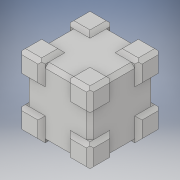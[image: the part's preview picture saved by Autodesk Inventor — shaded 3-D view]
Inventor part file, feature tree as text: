
AUTODESK INVENTOR PART (.ipt)
format: ipt  version: 2018 (Build 220112000, 112)  size: 468,480 bytes
history: native  units: in
note: dims shown in document units (in); Inventor stores cm internally (conversion verified against a paired STEP export)
features: chamfer x76, extrude x6, sketch x6
ambient origin geometry x8: Origin, YZ Plane, XZ Plane, XY Plane, X Axis, Y Axis, Z Axis, Center Point
bodies: Solid1 (feature_tree)
feature tree (88):
  extrude  "Extrusion1"  Depth=4.0in
  extrude  "Extrusion2"  Depth=1.3in
  extrude  "Extrusion3"  Depth=1.3in
  extrude  "Extrusion4"  Depth=1.3in
  extrude  "Extrusion5"  Depth=1.3in
  extrude  "Extrusion6"  Depth=1.3in
  chamfer  "Chamfer42"  Distance=1.3in
  chamfer  "Chamfer43"  Distance=1.3in
  chamfer  "Chamfer44"  Distance=1.3in
  chamfer  "Chamfer45"  Distance=0.2in
  chamfer  "Chamfer46"  Distance=0.2in
  chamfer  "Chamfer47"  Distance=0.2in
  chamfer  "Chamfer48"  Distance=0.2in
  chamfer  "Chamfer49"  Distance=0.2in Angle=45.0deg
  chamfer  "Chamfer50"  Distance=0.2in Angle=45.0deg
  chamfer  "Chamfer51"  Distance=0.2in Angle=45.0deg
  chamfer  "Chamfer52"  Distance=0.2in Angle=45.0deg
  chamfer  "Chamfer53"  Distance=0.2in Angle=45.0deg
  chamfer  "Chamfer54"  Distance=0.2in Angle=45.0deg
  chamfer  "Chamfer55"  Distance=0.2in Angle=45.0deg
  chamfer  "Chamfer56"  Distance=0.2in Angle=45.0deg
  chamfer  "Chamfer57"  Distance=0.2in Angle=45.0deg
  chamfer  "Chamfer58"  Distance=0.2in Angle=45.0deg
  chamfer  "Chamfer59"  Distance=0.2in Angle=45.0deg
  chamfer  "Chamfer60"  Distance=0.2in Angle=45.0deg
  chamfer  "Chamfer61"  Distance=0.2in Angle=45.0deg
  chamfer  "Chamfer62"  Distance=0.2in Angle=45.0deg
  chamfer  "Chamfer63"  Distance=0.2in Angle=45.0deg
  chamfer  "Chamfer64"  Distance=0.2in Angle=45.0deg
  chamfer  "Chamfer65"  Distance=0.2in Angle=45.0deg
  chamfer  "Chamfer66"  Distance=0.2in Angle=45.0deg
  chamfer  "Chamfer67"  Distance=0.2in Angle=45.0deg
  chamfer  "Chamfer68"  Distance=0.2in Angle=45.0deg
  chamfer  "Chamfer69"  Distance=0.2in Angle=45.0deg
  chamfer  "Chamfer70"  Distance=0.2in Angle=45.0deg
  chamfer  "Chamfer71"  Distance=0.2in Angle=45.0deg
  chamfer  "Chamfer72"  Distance=0.2in Angle=45.0deg
  chamfer  "Chamfer73"  Distance=0.2in Angle=45.0deg
  chamfer  "Chamfer74"  Distance=0.2in Angle=45.0deg
  chamfer  "Chamfer75"  Distance=0.2in Angle=45.0deg
  chamfer  "Chamfer76"  Distance=0.2in Angle=45.0deg
  chamfer  "Chamfer77"  Distance=0.2in Angle=45.0deg
  chamfer  "Chamfer78"  Distance=0.2in Angle=45.0deg
  chamfer  "Chamfer79"  Distance=0.2in Angle=45.0deg
  chamfer  "Chamfer80"  Distance=0.2in Angle=45.0deg
  chamfer  "Chamfer81"  Distance=0.2in Angle=45.0deg
  chamfer  "Chamfer82"  Distance=0.2in Angle=45.0deg
  chamfer  "Chamfer83"  Distance=0.2in Angle=45.0deg
  chamfer  "Chamfer84"  Distance=0.2in Angle=45.0deg
  chamfer  "Chamfer85"  Distance=0.2in Angle=45.0deg
  chamfer  "Chamfer86"  Distance=0.2in Angle=45.0deg
  chamfer  "Chamfer87"  Distance=0.2in Angle=45.0deg
  chamfer  "Chamfer88"  Distance=0.2in Angle=45.0deg
  chamfer  "Chamfer89"  Distance=0.2in Angle=45.0deg
  chamfer  "Chamfer90"  Distance=0.2in Angle=45.0deg
  chamfer  "Chamfer91"  Distance=0.2in Angle=45.0deg
  chamfer  "Chamfer92"  Distance=0.2in Angle=45.0deg
  chamfer  "Chamfer93"  Distance=0.2in Angle=45.0deg
  chamfer  "Chamfer94"  Distance=0.2in Angle=45.0deg
  chamfer  "Chamfer95"  Distance=0.2in Angle=45.0deg
  chamfer  "Chamfer96"  Distance=0.2in Angle=45.0deg
  chamfer  "Chamfer97"  Distance=0.2in Angle=45.0deg
  chamfer  "Chamfer98"  Distance=0.2in Angle=45.0deg
  chamfer  "Chamfer99"  Distance=0.2in Angle=45.0deg
  chamfer  "Chamfer100"  Distance=0.2in Angle=45.0deg
  chamfer  "Chamfer101"  Distance=0.2in Angle=45.0deg
  chamfer  "Chamfer102"  Distance=0.2in Angle=45.0deg
  chamfer  "Chamfer103"  Distance=0.2in Angle=45.0deg
  chamfer  "Chamfer104"  Distance=0.2in Angle=45.0deg
  chamfer  "Chamfer105"  Distance=0.2in Angle=45.0deg
  chamfer  "Chamfer106"  Distance=0.2in Angle=45.0deg
  chamfer  "Chamfer107"  Distance=0.2in Angle=45.0deg
  chamfer  "Chamfer108"  Distance=0.2in Angle=45.0deg
  chamfer  "Chamfer109"  Distance=0.2in Angle=45.0deg
  chamfer  "Chamfer110"  Distance=0.2in Angle=45.0deg
  chamfer  "Chamfer111"  Distance=0.2in Angle=45.0deg
  chamfer  "Chamfer112"  Distance=0.2in Angle=45.0deg
  chamfer  "Chamfer113"  Distance=0.2in Angle=45.0deg
  chamfer  "Chamfer114"  Distance=0.2in Angle=45.0deg
  chamfer  "Chamfer115"  Distance=0.2in Angle=45.0deg
  chamfer  "Chamfer116"  Distance=0.2in Angle=45.0deg
  chamfer  "Chamfer117"  Distance=0.2in Angle=45.0deg
  sketch  "Sketch1"  dims[d0=4.0in d1=4.0in]
  sketch  "Sketch2"  dims[d2=4.0in d3=0.0in d4=1.3in]
  sketch  "Sketch3"  dims[d5=1.3in d6=1.3in]
  sketch  "Sketch4"  dims[d7=1.3in d8=1.3in]
  sketch  "Sketch5"  dims[d9=1.3in d10=1.3in]
  sketch  "Sketch6"  dims[d11=0.2in d12=0.0in d13=1.3in d14=1.3in d15=1.3in d16=1.3in d17=0.2in d18=0.0in d19=0.2in d20=0.0in d21=0.2in d22=0.0in d23=0.2in d24=0.0in d148=0.2in d149=0.2in d150=45.0deg d151=0.2in d152=0.2in d153=45.0deg d154=0.2in d155=0.2in d156=45.0deg d157=0.2in d158=0.2in d159=45.0deg d160=0.2in d161=0.2in d162=45.0deg d163=0.2in d164=0.2in d165=45.0deg d166=0.2in d167=0.2in d168=45.0deg d169=0.2in d170=0.2in d171=45.0deg d172=0.2in d173=0.2in d174=45.0deg d175=0.2in d176=0.2in d177=45.0deg d178=0.2in d179=0.2in d180=45.0deg d181=0.2in d182=0.2in d183=45.0deg d184=0.2in d185=0.2in d186=45.0deg d187=0.2in d188=0.2in d189=45.0deg d190=0.2in d191=0.2in d192=45.0deg d193=0.2in d194=0.2in d195=45.0deg d196=0.2in d197=0.2in d198=45.0deg d199=0.2in d200=0.2in d201=45.0deg d202=0.2in d203=0.2in d204=45.0deg d205=0.2in d206=0.2in d207=45.0deg d208=0.2in d209=0.2in d210=45.0deg d211=0.2in d212=0.2in d213=45.0deg d214=0.2in d215=0.2in d216=45.0deg d217=0.2in d218=0.2in d219=45.0deg d220=0.2in d221=0.2in d222=45.0deg d223=0.2in d224=0.2in d225=45.0deg d226=0.2in d227=0.2in d228=45.0deg d229=0.2in d230=0.2in d231=45.0deg d232=0.2in d233=0.2in d234=45.0deg d235=0.2in d236=0.2in d237=45.0deg d238=0.2in d239=0.2in d240=45.0deg d241=0.2in d242=0.2in d243=45.0deg d244=0.2in d245=0.2in d246=45.0deg d247=0.2in d248=0.2in d249=45.0deg d250=0.2in d251=0.2in d252=45.0deg d253=0.2in d254=0.2in d255=45.0deg d256=0.2in d257=0.2in d258=45.0deg d259=0.2in d260=0.2in d261=45.0deg d262=0.2in d263=0.2in d264=45.0deg d265=0.2in d266=0.2in d267=45.0deg d268=0.2in d269=0.2in d270=45.0deg d271=0.2in d272=0.2in d273=45.0deg d274=0.2in d275=0.2in d276=45.0deg d277=0.2in d278=0.2in d279=45.0deg d280=0.2in d281=0.2in d282=45.0deg d283=0.2in d284=0.2in d285=45.0deg d286=0.2in d287=0.2in d288=45.0deg d289=0.2in d290=0.2in d291=45.0deg d292=0.2in d293=0.2in d294=45.0deg d295=0.2in d296=0.2in d297=45.0deg d298=0.2in d299=0.2in d300=45.0deg d301=0.2in d302=0.2in d303=45.0deg d304=0.2in d305=0.2in d306=45.0deg d307=0.2in d308=0.2in d309=45.0deg d310=0.2in d311=0.2in d312=45.0deg d313=0.2in d314=0.2in d315=45.0deg d316=0.2in d317=0.2in d318=45.0deg d319=0.2in d320=0.2in d321=45.0deg d322=0.2in d323=0.2in d324=45.0deg d325=0.2in d326=0.2in d327=45.0deg d328=0.2in d329=0.2in d330=45.0deg d331=0.2in d332=0.2in d333=45.0deg d334=0.2in d335=0.2in d336=45.0deg d337=0.2in d338=0.2in d339=45.0deg d340=0.2in d341=0.2in d342=45.0deg d343=0.2in d344=0.2in d345=45.0deg d346=0.2in d347=0.2in d348=45.0deg d349=0.2in d350=0.2in d351=45.0deg d352=0.2in d353=0.2in d354=45.0deg d355=0.2in d356=0.2in d357=45.0deg d358=0.2in d359=0.2in d360=45.0deg d361=0.2in d362=0.2in d363=45.0deg d364=0.2in d365=0.2in d366=45.0deg d367=0.2in d368=0.2in d369=45.0deg d370=0.2in d371=0.2in d372=45.0deg d373=0.2in d374=0.2in d375=45.0deg]
